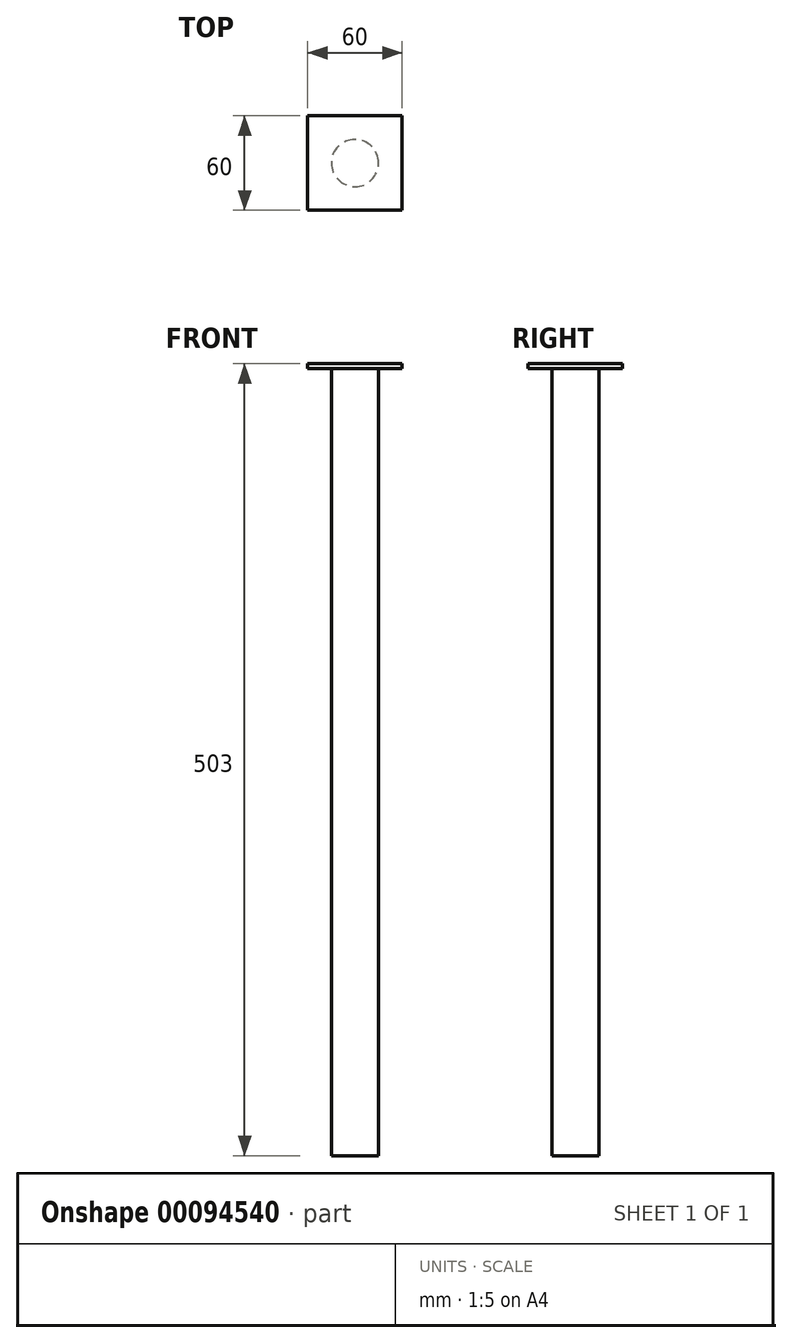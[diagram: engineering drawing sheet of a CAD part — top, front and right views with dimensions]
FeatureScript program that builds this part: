
annotation { "Feature Type Name" : "Feature", "Feature Type Description" : "" }
export const myFeature = defineFeature(function(context is Context, id is Id, definition is map)
    precondition{}
    {
        {
            var Q0;
            Q0=qCreatedBy(makeId("Top.planeOp"),FACE);
            var sketch = newSketch(context, id + "F0", { "sketchPlane" : qUnion([Q0])});
            skCircle(sketch, "E0", {"center": v(0, 0) * mm, "radius": 15 * mm});
            skSolve(sketch);
        }
        {
            var Q0;
            Q0=makeQuery(id+"F0.imprint","IMPRINT",FACE,{"disambiguationData":[TD([[makeQuery(id+"F0.imprint","IMPRINT",EDGE,{"derivedFrom":sQuery(id+"F0.wireOp",EDGE,"E0")}),1.0]])]});
            extrude(context, id + "F1", {"entities" : qUnion([Q0]), "depth" : 500 * mm});
        }
        {
            var Q0;
            Q0=makeQuery(id+"F1.opExtrude","CAP_FACE",FACE,{"disambiguationData":[OSD([sQuery(id+"F0.wireOp",EDGE,"E0")])],"isStart":false});
            var sketch = newSketch(context, id + "F2", { "sketchPlane" : qUnion([Q0])});
            skLineSegment(sketch, "E1.bottom", {"start": v(30, -30) * mm, "end": v(-30, -30) * mm});
            skLineSegment(sketch, "E1.top", {"start": v(30, 30) * mm, "end": v(-30, 30) * mm});
            skLineSegment(sketch, "E1.left", {"start": v(30, -30) * mm, "end": v(30, 30) * mm});
            skLineSegment(sketch, "E1.right", {"start": v(-30, -30) * mm, "end": v(-30, 30) * mm});
            skPoint(sketch, "E1.middle", {"position": v(0, 0) * mm});
            skSolve(sketch);
        }
        {
            var Q0;
            Q0 = qSketchRegion(id + "F2", true);
            var Q1;
            Q1=makeQuery(id+"F2.imprint","IMPRINT",FACE,{"disambiguationData":[TD([[makeQuery(id+"F2.imprint","IMPRINT",EDGE,{"derivedFrom":sQuery(id+"F2.wireOp",EDGE,"E1.bottom")}),-1.0]])]});
            extrude(context, id + "F3", {"entities" : qUnion([Q0, Q1]), "operationType" : NewBodyOperationType.ADD, "depth" : 3 * mm});
        }
    });
